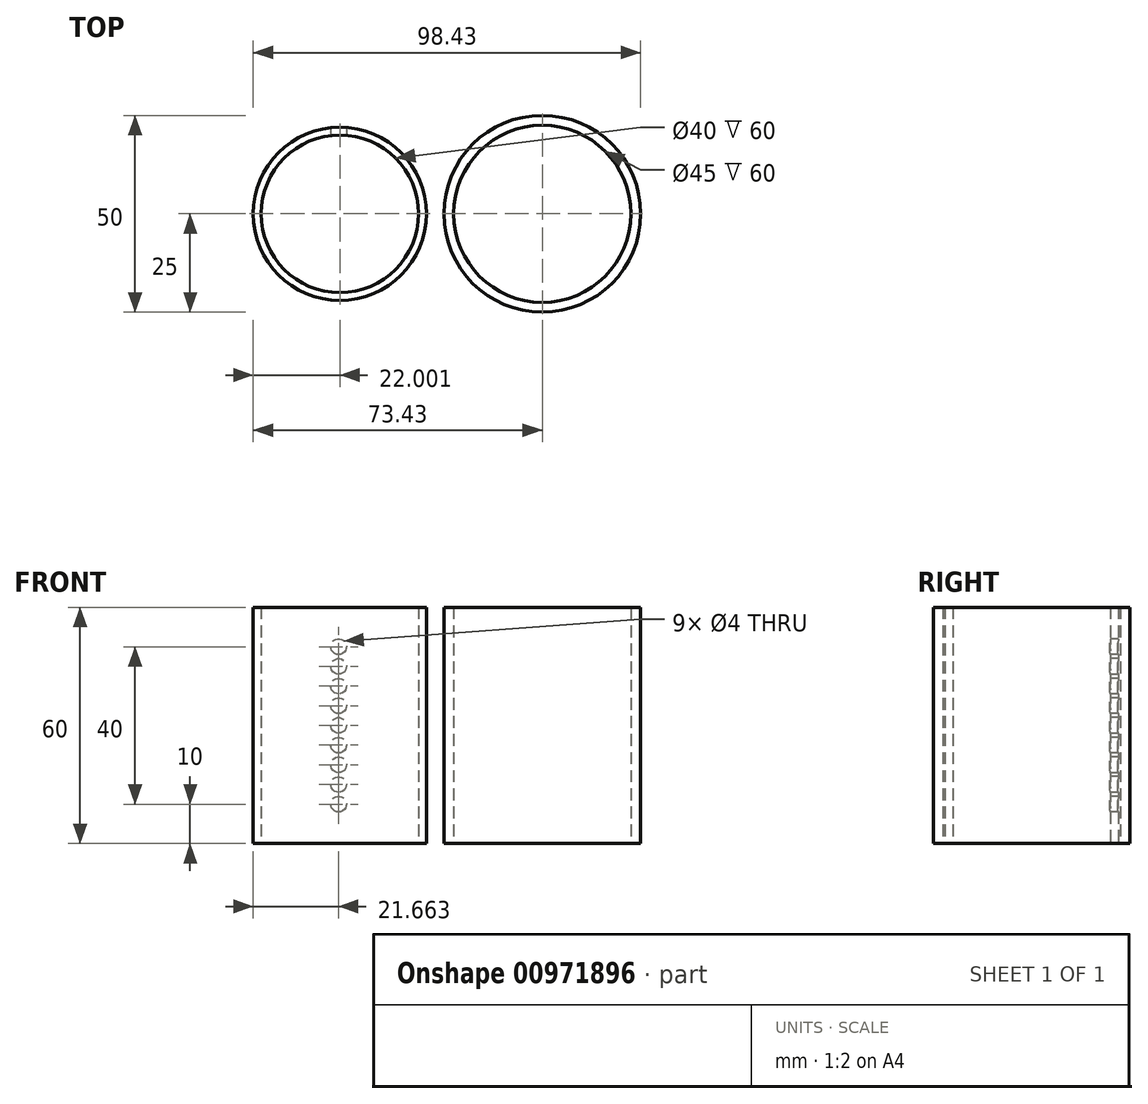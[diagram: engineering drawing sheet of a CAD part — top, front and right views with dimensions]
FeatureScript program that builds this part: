
annotation { "Feature Type Name" : "Feature", "Feature Type Description" : "" }
export const myFeature = defineFeature(function(context is Context, id is Id, definition is map)
    precondition{}
    {
        {
            var Q0;
            Q0=qCreatedBy(makeId("Top.planeOp"),FACE);
            var sketch = newSketch(context, id + "F0", { "sketchPlane" : qUnion([Q0])});
            skCircle(sketch, "E0", {"center": v(0, 0) * mm, "radius": 25 * mm});
            skCircle(sketch, "E1", {"center": v(0, 0) * mm, "radius": 22.5 * mm});
            skSolve(sketch);
        }
        {
            var Q0;
            Q0=makeQuery(id+"F0.imprint","IMPRINT",FACE,{"disambiguationData":[TD([[makeQuery(id+"F0.imprint","IMPRINT",EDGE,{"derivedFrom":sQuery(id+"F0.wireOp",EDGE,"E0")}),1.0]])]});
            extrude(context, id + "F1", {"entities" : qUnion([Q0]), "depth" : 60 * mm, "offsetDistance" : 25 * mm});
        }
        {
            var Q0;
            Q0=qCreatedBy(makeId("Top.planeOp"),FACE);
            var sketch = newSketch(context, id + "F2", { "sketchPlane" : qUnion([Q0])});
            skCircle(sketch, "E2", {"center": v(-51.43, 0) * mm, "radius": 22 * mm});
            skCircle(sketch, "E3", {"center": v(-51.43, 0) * mm, "radius": 20 * mm});
            skSolve(sketch);
        }
        {
            var Q0;
            Q0=makeQuery(id+"F2.imprint","IMPRINT",FACE,{"disambiguationData":[TD([[makeQuery(id+"F2.imprint","IMPRINT",EDGE,{"derivedFrom":sQuery(id+"F2.wireOp",EDGE,"E2")}),1.0]])]});
            extrude(context, id + "F3", {"entities" : qUnion([Q0]), "depth" : 60 * mm, "offsetDistance" : 25 * mm});
        }
        {
            var Q0;
            Q0=qCreatedBy(makeId("Front.planeOp"),FACE);
            var sketch = newSketch(context, id + "F4", { "sketchPlane" : qUnion([Q0])});
            skPoint(sketch, "E4", {"position": v(-51.77, 50) * mm});
            skPoint(sketch, "E5", {"position": v(-51.77, 40) * mm});
            skPoint(sketch, "E6", {"position": v(-51.77, 30) * mm});
            skPoint(sketch, "E7", {"position": v(-51.77, 20) * mm});
            skPoint(sketch, "E8", {"position": v(-51.77, 10) * mm});
            skPoint(sketch, "E9", {"position": v(-51.77, 15) * mm});
            skPoint(sketch, "E10", {"position": v(-51.77, 25) * mm});
            skPoint(sketch, "E11", {"position": v(-51.77, 35) * mm});
            skPoint(sketch, "E12", {"position": v(-51.77, 45) * mm});
            skSolve(sketch);
        }
        {
            var Q0;
            Q0=sQuery(id+"F4.wireOp",VERTEX,"E4");
            var Q1;
            Q1=sQuery(id+"F4.wireOp",VERTEX,"E12");
            var Q2;
            Q2=sQuery(id+"F4.wireOp",VERTEX,"E5");
            var Q3;
            Q3=sQuery(id+"F4.wireOp",VERTEX,"E11");
            var Q4;
            Q4=sQuery(id+"F4.wireOp",VERTEX,"E6");
            var Q5;
            Q5=sQuery(id+"F4.wireOp",VERTEX,"E10");
            var Q6;
            Q6=sQuery(id+"F4.wireOp",VERTEX,"E7");
            var Q7;
            Q7=sQuery(id+"F4.wireOp",VERTEX,"E9");
            var Q8;
            Q8=sQuery(id+"F4.wireOp",VERTEX,"E8");
            var Q9;
            Q9=makeQuery(id+"F3.opExtrude","SWEPT_BODY",BODY,{"disambiguationData":[OSD([sQuery(id+"F2.wireOp",EDGE,"E2"),sQuery(id+"F2.wireOp",EDGE,"E3")])]});
            hole(context, id + "F5", {"style" : HoleStyle.SIMPLE, "endStyle" : HoleEndStyle.THROUGH, "holeDiameter" : 4 * mm, "majorDiameter" : 5 * mm, "isTappedThrough" : true, "tappedDepth" : 12 * mm, "tapClearance" : 3, "locations" : qUnion([Q0, Q1, Q2, Q3, Q4, Q5, Q6, Q7, Q8]), "scope" : qUnion([Q9])});
        }
    });
